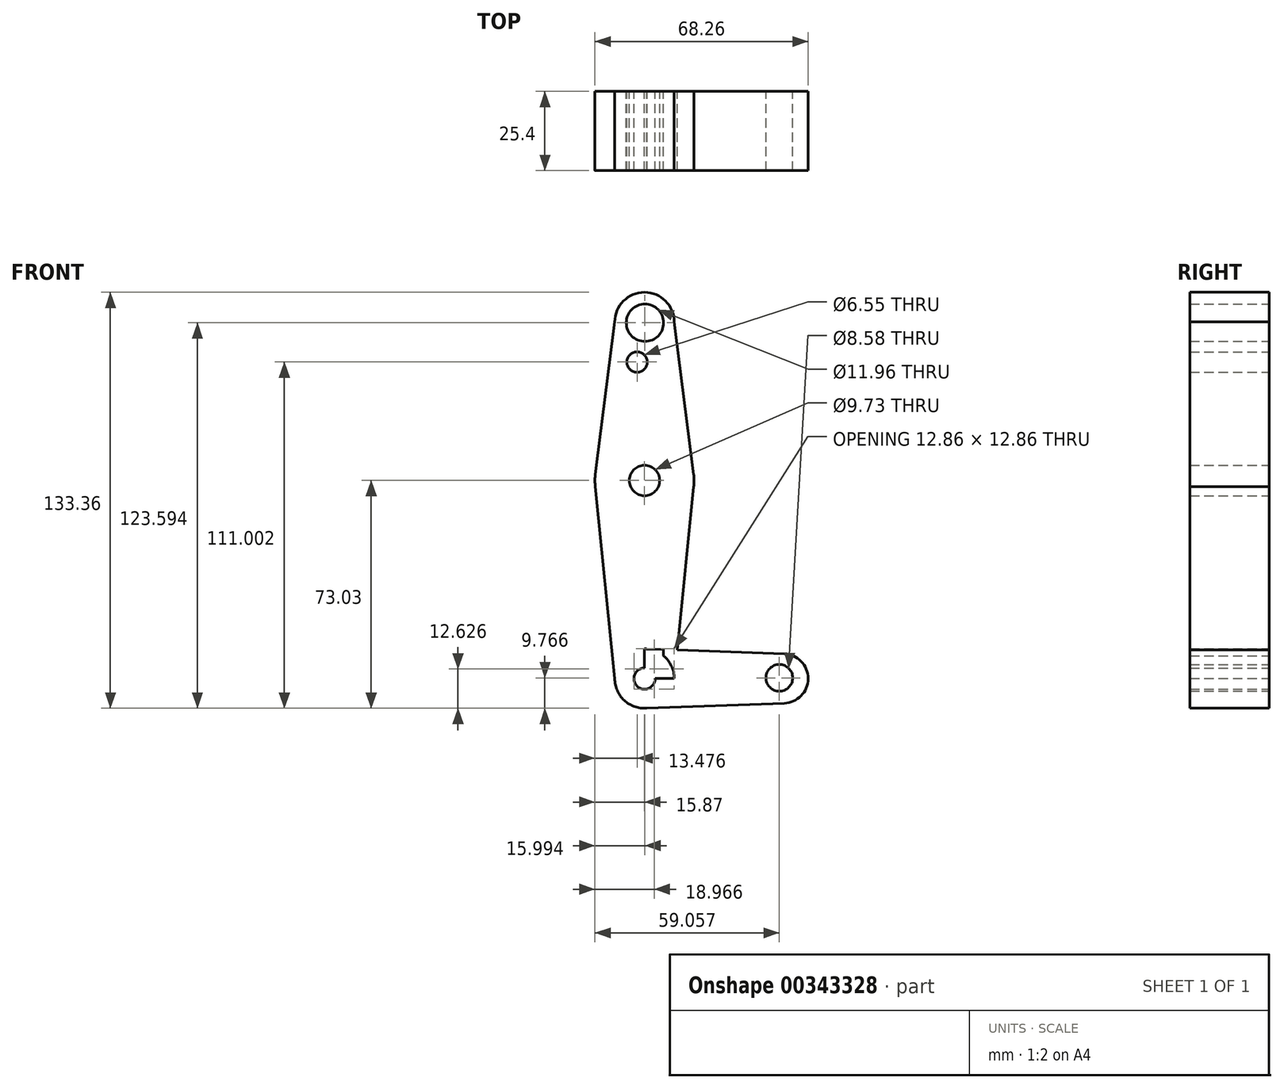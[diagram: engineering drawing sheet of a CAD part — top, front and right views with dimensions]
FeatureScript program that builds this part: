
annotation { "Feature Type Name" : "Feature", "Feature Type Description" : "" }
export const myFeature = defineFeature(function(context is Context, id is Id, definition is map)
    precondition{}
    {
        {
            var Q0;
            Q0=qCreatedBy(makeId("Front.planeOp"),FACE);
            var sketch = newSketch(context, id + "F0", { "sketchPlane" : qUnion([Q0])});
            skLineSegment(sketch, "E0", {"start": v(0, 114.3) * mm, "end": v(0, 0) * mm});
            skCircle(sketch, "E1", {"center": v(0, 114.3) * mm, "radius": 9.53 * mm});
            skCircle(sketch, "E2", {"center": v(0, 63.5) * mm, "radius": 15.88 * mm});
            skCircle(sketch, "E3", {"center": v(0, 0) * mm, "radius": 9.53 * mm});
            skLineSegment(sketch, "E4", {"start": v(0, 0) * mm, "end": v(44.45, 0) * mm});
            skCircle(sketch, "E5", {"center": v(44.45, 0) * mm, "radius": 7.94 * mm});
            skLineSegment(sketch, "E6", {"start": v(0, 9.52) * mm, "end": v(44.73, 7.93) * mm});
            skLineSegment(sketch, "E7", {"start": v(0, -9.53) * mm, "end": v(44.73, -7.93) * mm});
            skLineSegment(sketch, "E8", {"start": v(6.1, 7.31) * mm, "end": v(6.1, 9.3) * mm});
            skLineSegment(sketch, "E9", {"start": v(9.52, 114.3) * mm, "end": v(15.75, 65.5) * mm});
            skLineSegment(sketch, "E10", {"start": v(-9.53, 114.3) * mm, "end": v(-15.75, 65.5) * mm});
            skLineSegment(sketch, "E11", {"start": v(15.75, 61.5) * mm, "end": v(9.52, 0) * mm});
            skCircle(sketch, "E12", {"center": v(0, 63.5) * mm, "radius": 4.87 * mm});
            skCircle(sketch, "E13", {"center": v(0.12, 114.06) * mm, "radius": 5.98 * mm});
            skCircle(sketch, "E14", {"center": v(-2.4, 101.47) * mm, "radius": 3.27 * mm});
            skCircle(sketch, "E15", {"center": v(0, 0) * mm, "radius": 3.4 * mm});
            skCircle(sketch, "E16", {"center": v(43.19, 0.24) * mm, "radius": 4.29 * mm});
            skLineSegment(sketch, "E17", {"start": v(-9.52, 0) * mm, "end": v(-15.75, 61.5) * mm});
            skSolve(sketch);
        }
        {
            var Q0;
            Q0 = qSketchRegion(id + "F0", true);
            extrude(context, id + "F1", {"entities" : qUnion([Q0]), "depth" : 25.4 * mm});
        }
    });
